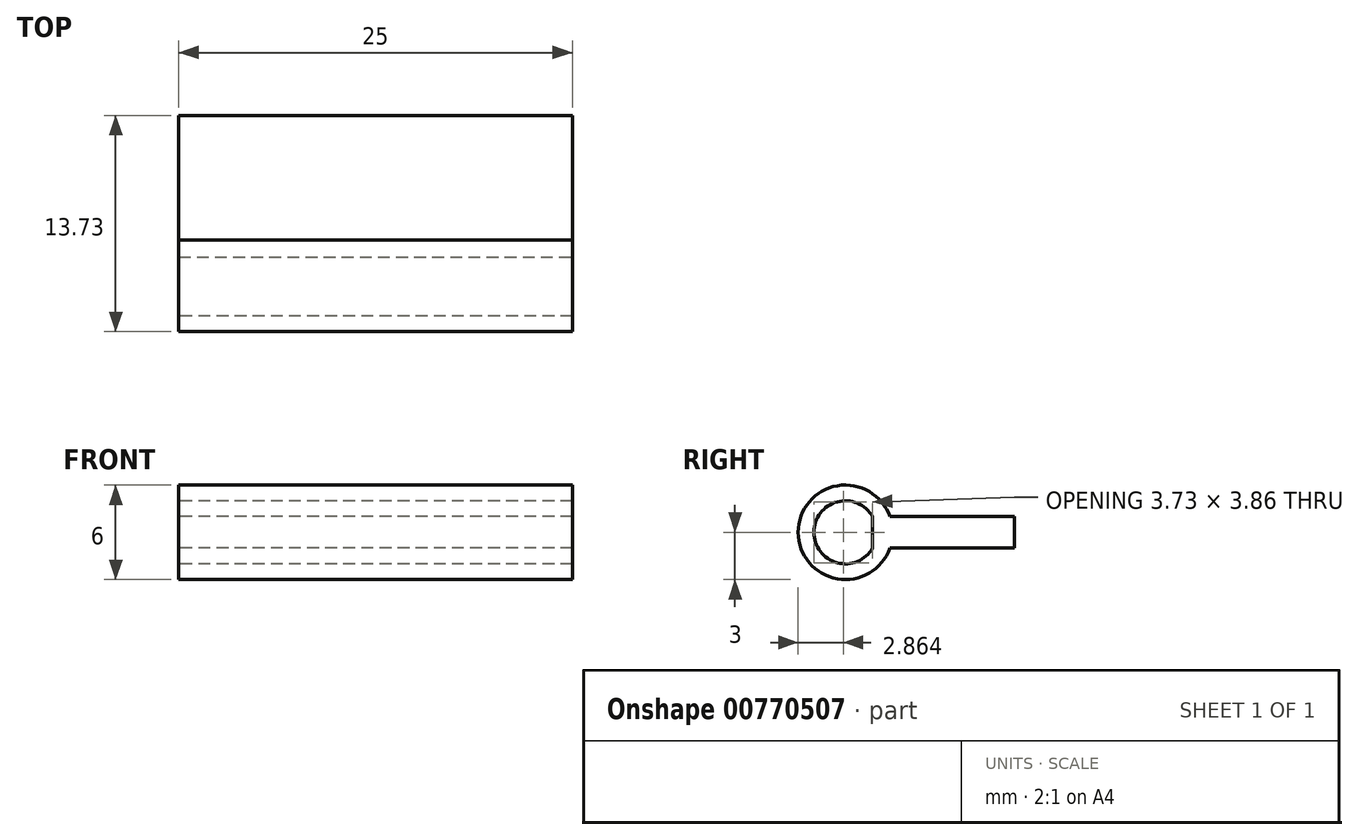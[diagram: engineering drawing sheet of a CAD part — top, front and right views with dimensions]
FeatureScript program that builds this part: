
annotation { "Feature Type Name" : "Feature", "Feature Type Description" : "" }
export const myFeature = defineFeature(function(context is Context, id is Id, definition is map)
    precondition{}
    {
        {
            var Q0;
            Q0=qCreatedBy(makeId("Top.planeOp"),FACE);
            var sketch = newSketch(context, id + "F0", { "sketchPlane" : qUnion([Q0])});
            skLineSegment(sketch, "E0.bottom", {"start": v(-12.5, -4.5) * mm, "end": v(12.5, -4.5) * mm});
            skLineSegment(sketch, "E0.top", {"start": v(-12.5, 4.5) * mm, "end": v(12.5, 4.5) * mm});
            skLineSegment(sketch, "E0.left", {"start": v(-12.5, -4.5) * mm, "end": v(-12.5, 4.5) * mm});
            skLineSegment(sketch, "E0.right", {"start": v(12.5, -4.5) * mm, "end": v(12.5, 4.5) * mm});
            skSolve(sketch);
        }
        {
            var Q0;
            Q0=makeQuery(id+"F0.imprint","IMPRINT",FACE,{"disambiguationData":[TD([[makeQuery(id+"F0.imprint","IMPRINT",EDGE,{"derivedFrom":sQuery(id+"F0.wireOp",EDGE,"E0.bottom")}),1.0]])]});
            extrude(context, id + "F1", {"entities" : qUnion([Q0]), "depth" : 2 * mm, "offsetDistance" : 25 * mm});
        }
        {
            var Q0;
            Q0=qCreatedBy(makeId("Right.planeOp"),FACE);
            var sketch = newSketch(context, id + "F2", { "sketchPlane" : qUnion([Q0])});
            skArc(sketch, "E1", {"start": v(-3.4, 2) * mm, "mid": v(-9.23, 1) * mm, "end": v(-3.4, 0) * mm});
            skLineSegment(sketch, "E2", {"start": v(-6.23, 1) * mm, "end": v(34.76, 1) * mm, "construction": true});
            skArc(sketch, "E3", {"start": v(-4.5, 2) * mm, "mid": v(-8.23, 1) * mm, "end": v(-4.5, 0) * mm});
            skLineSegment(sketch, "E4", {"start": v(-3.4, 2) * mm, "end": v(-4.5, 2) * mm});
            skLineSegment(sketch, "E5", {"start": v(-4.5, 2) * mm, "end": v(-4.5, 1) * mm});
            skLineSegment(sketch, "E6", {"start": v(-4.5, 0) * mm, "end": v(-3.4, 0) * mm});
            skLineSegment(sketch, "E7", {"start": v(-4.5, 1) * mm, "end": v(-4.5, 0) * mm});
            skSolve(sketch);
        }
        {
            var Q0;
            Q0=makeQuery(id+"F2.imprint","IMPRINT",FACE,{"disambiguationData":[TD([[makeQuery(id+"F2.imprint","IMPRINT",EDGE,{"derivedFrom":sQuery(id+"F2.wireOp",EDGE,"E1")}),1.0]])]});
            extrude(context, id + "F3", {"entities" : qUnion([Q0]), "operationType" : NewBodyOperationType.ADD, "depth" : 12.5 * mm, "offsetDistance" : 25 * mm, "hasSecondDirection" : true, "secondDirectionOppositeDirection" : true, "secondDirectionDepth" : 12.5 * mm});
        }
    });
